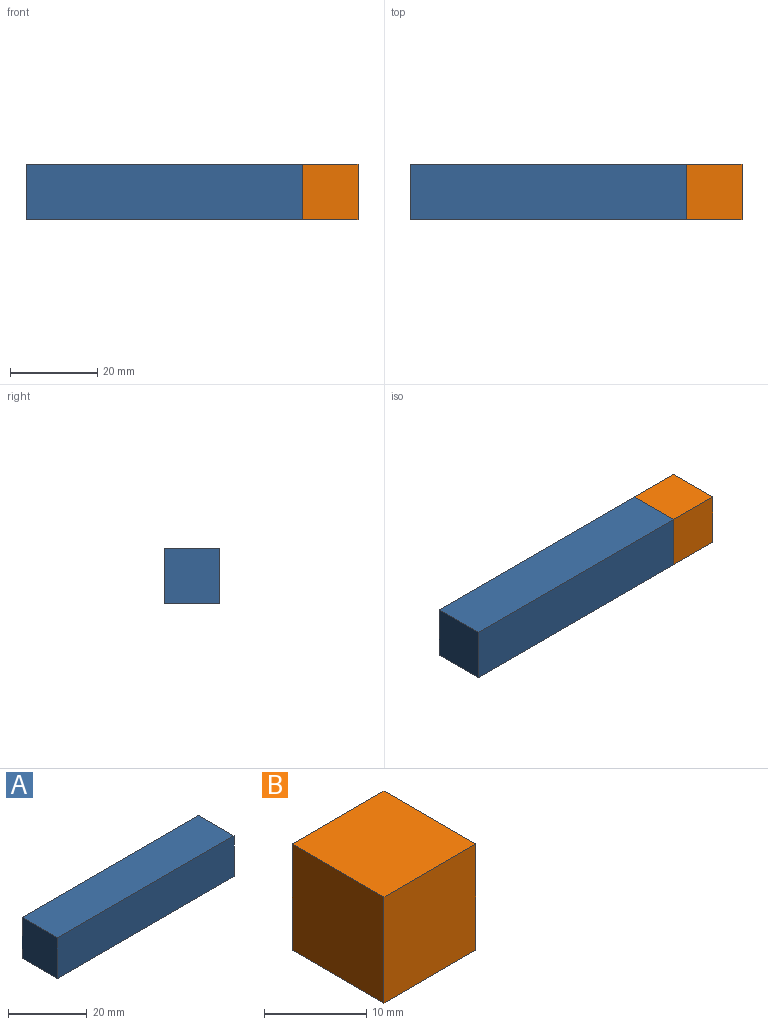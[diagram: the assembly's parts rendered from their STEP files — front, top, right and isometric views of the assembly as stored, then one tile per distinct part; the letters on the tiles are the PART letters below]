
ASSEMBLY  parts=2 mates=1
PART A: 6 faces, bbox 63.5x12.7x12.7 mm
  f0: plane 63.5x12.7mm, normal (0,0,-1), area 806.5mm2, adj f1,f3,f4,f5
  f1: plane 12.7x12.7mm, normal (1,0,0), area 161.3mm2, adj f0,f2,f4,f5
  f2: plane 63.5x12.7mm, normal (0,0,1), area 806.5mm2, adj f1,f3,f4,f5
  f3: plane 12.7x12.7mm, normal (-1,0,0), area 161.3mm2, adj f0,f2,f4,f5
  f4: plane 63.5x12.7mm, normal (0,-1,0), area 806.5mm2, adj f0,f1,f2,f3
  f5: plane 63.5x12.7mm, normal (0,1,0), area 806.5mm2, adj f0,f1,f2,f3
PART B: 6 faces, bbox 12.7x12.7x12.7 mm
  f0: plane 12.7x12.7mm, normal (0,0,-1), area 161.3mm2, adj f1,f3,f4,f5
  f1: plane 12.7x12.7mm, normal (1,0,0), area 161.3mm2, adj f0,f2,f4,f5
  f2: plane 12.7x12.7mm, normal (0,0,1), area 161.3mm2, adj f1,f3,f4,f5
  f3: plane 12.7x12.7mm, normal (-1,0,0), area 161.3mm2, adj f0,f2,f4,f5
  f4: plane 12.7x12.7mm, normal (0,-1,0), area 161.3mm2, adj f0,f1,f2,f3
  f5: plane 12.7x12.7mm, normal (0,1,0), area 161.3mm2, adj f0,f1,f2,f3
PLACE A t=(-72.03,-2.35,34.51)mm
PLACE B t=(-37.24,-2.35,-37.67)mm
MATE fastened A.f1 <-> B.f3  axis (1,0,0) through (-43.59,-8.7,-9.1)mm
